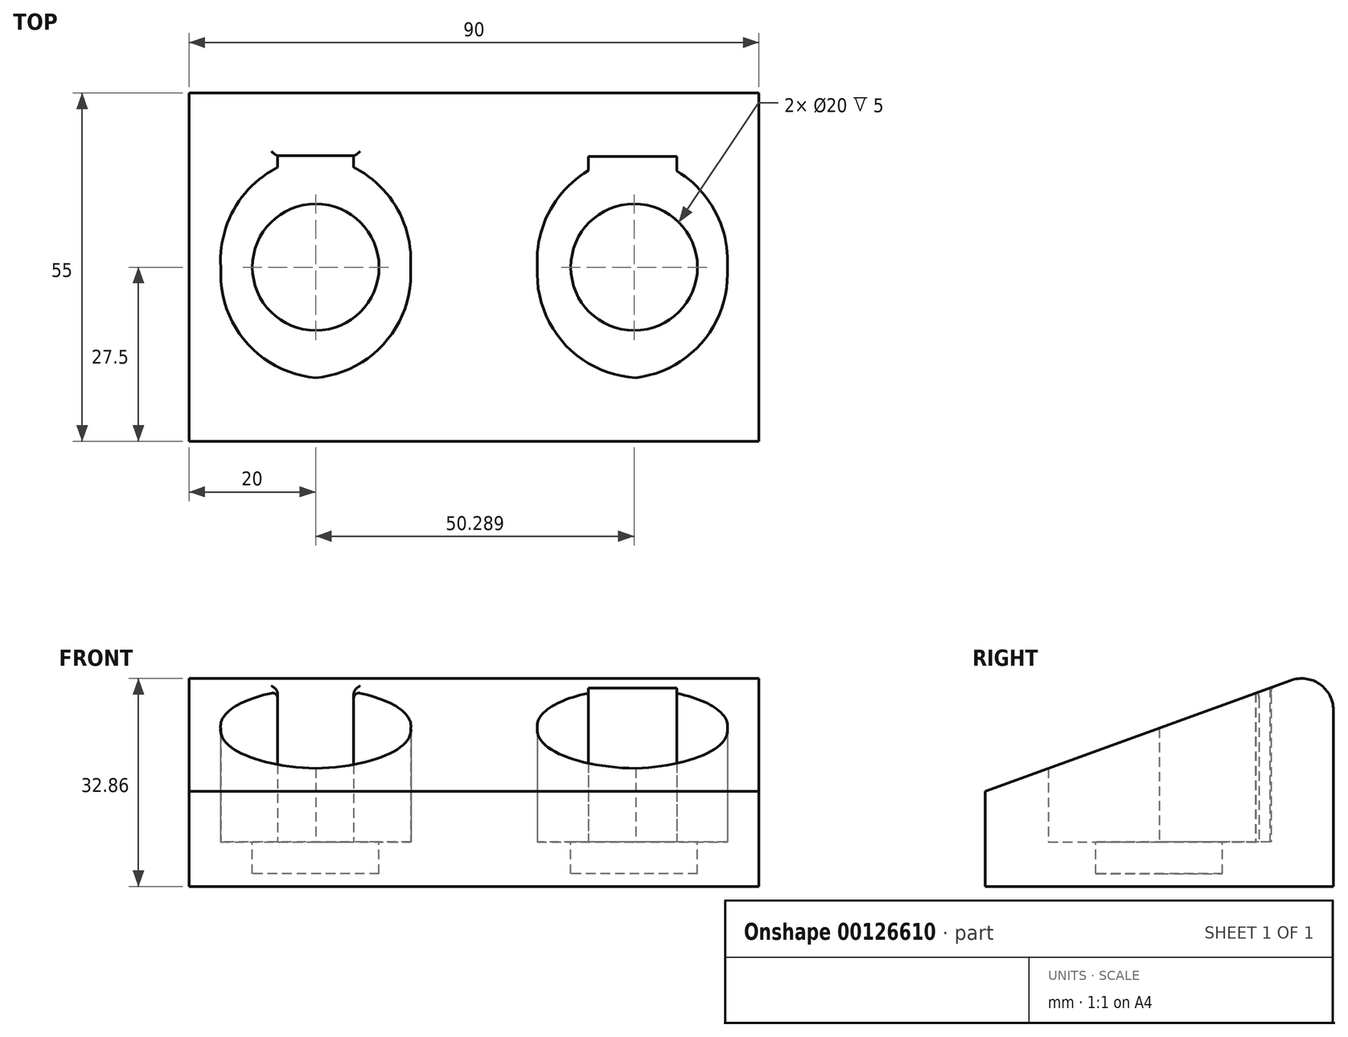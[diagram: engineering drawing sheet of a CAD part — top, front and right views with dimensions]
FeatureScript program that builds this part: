
annotation { "Feature Type Name" : "Feature", "Feature Type Description" : "" }
export const myFeature = defineFeature(function(context is Context, id is Id, definition is map)
    precondition{}
    {
        {
            var Q0;
            Q0=qCreatedBy(makeId("Top.planeOp"),FACE);
            var sketch = newSketch(context, id + "F0", { "sketchPlane" : qUnion([Q0])});
            skLineSegment(sketch, "E0", {"start": v(0, 0) * mm, "end": v(-25, 0) * mm, "construction": true});
            skLineSegment(sketch, "E1", {"start": v(0, 0) * mm, "end": v(25, 0) * mm, "construction": true});
            skLineSegment(sketch, "E2", {"start": v(-25, 0) * mm, "end": v(-10, 0) * mm, "construction": true});
            skLineSegment(sketch, "E3", {"start": v(-25, 0) * mm, "end": v(-25, 24.58) * mm, "construction": true});
            skLineSegment(sketch, "E4", {"start": v(-25, 0) * mm, "end": v(-25, -21.82) * mm, "construction": true});
            skArc(sketch, "E5", {"start": v(-25, 17.5) * mm, "mid": v(-36.06, 11.8) * mm, "end": v(-40, 0) * mm});
            skArc(sketch, "E6", {"start": v(-40, 0) * mm, "mid": v(-36.06, -11.8) * mm, "end": v(-25, -17.5) * mm});
            skArc(sketch, "E7", {"start": v(-10, 0) * mm, "mid": v(-13.94, 11.8) * mm, "end": v(-25, 17.5) * mm});
            skArc(sketch, "E8", {"start": v(-25, -17.5) * mm, "mid": v(-13.94, -11.8) * mm, "end": v(-10, 0) * mm});
            skLineSegment(sketch, "E9", {"start": v(-25, 17.5) * mm, "end": v(32.65, 17.5) * mm, "construction": true});
            skLineSegment(sketch, "E10", {"start": v(-25, -17.5) * mm, "end": v(35.4, -17.5) * mm, "construction": true});
            skLineSegment(sketch, "E11", {"start": v(25, 0) * mm, "end": v(25, 19.84) * mm, "construction": true});
            skLineSegment(sketch, "E12", {"start": v(25, 19.84) * mm, "end": v(25.58, -19.79) * mm, "construction": true});
            skArc(sketch, "E13", {"start": v(25.03, 17.5) * mm, "mid": v(13.95, 11.81) * mm, "end": v(10, 0) * mm});
            skArc(sketch, "E14", {"start": v(10, 0) * mm, "mid": v(14.13, -11.98) * mm, "end": v(25.54, -17.5) * mm});
            skArc(sketch, "E15", {"start": v(40, 0) * mm, "mid": v(36.07, 11.8) * mm, "end": v(25.03, 17.5) * mm});
            skArc(sketch, "E16", {"start": v(25.54, -17.5) * mm, "mid": v(36.26, -11.63) * mm, "end": v(40, 0) * mm});
            skLineSegment(sketch, "E17", {"start": v(0, 0) * mm, "end": v(-45, 0) * mm, "construction": true});
            skLineSegment(sketch, "E18", {"start": v(-45, 0) * mm, "end": v(-45, -27.5) * mm, "construction": true});
            skLineSegment(sketch, "E19", {"start": v(-45, 0) * mm, "end": v(-45, 27.5) * mm, "construction": true});
            skLineSegment(sketch, "E20", {"start": v(0, 0) * mm, "end": v(45, 0) * mm, "construction": true});
            skLineSegment(sketch, "E21", {"start": v(45, 0) * mm, "end": v(45, 27.5) * mm, "construction": true});
            skLineSegment(sketch, "E22.bottom", {"start": v(-45, -27.5) * mm, "end": v(45, -27.5) * mm});
            skLineSegment(sketch, "E22.top", {"start": v(-45, 27.5) * mm, "end": v(45, 27.5) * mm});
            skLineSegment(sketch, "E22.left", {"start": v(-45, -27.5) * mm, "end": v(-45, 27.5) * mm});
            skLineSegment(sketch, "E22.right", {"start": v(45, -27.5) * mm, "end": v(45, 27.5) * mm});
            skSolve(sketch);
        }
        {
            var Q0;
            Q0=makeQuery(id+"F0.imprint","IMPRINT",FACE,{"disambiguationData":[TD([[makeQuery(id+"F0.imprint","IMPRINT",EDGE,{"derivedFrom":sQuery(id+"F0.wireOp",EDGE,"E5")}),-1.0]])]});
            extrude(context, id + "F1", {"entities" : qUnion([Q0]), "depth" : 35 * mm});
        }
        {
            var Q0;
            Q0=makeQuery(id+"F0.imprint","IMPRINT",FACE,{"disambiguationData":[TD([[makeQuery(id+"F0.imprint","IMPRINT",EDGE,{"derivedFrom":sQuery(id+"F0.wireOp",EDGE,"E5")}),1.0]])]});
            var Q1;
            Q1=makeQuery(id+"F0.imprint","IMPRINT",FACE,{"disambiguationData":[TD([[makeQuery(id+"F0.imprint","IMPRINT",EDGE,{"derivedFrom":sQuery(id+"F0.wireOp",EDGE,"E13")}),1.0]])]});
            extrude(context, id + "F2", {"entities" : qUnion([Q0, Q1]), "operationType" : NewBodyOperationType.ADD, "depth" : 7 * mm});
        }
        {
            var Q0;
            Q0=makeQuery(id+"F2.opExtrude","CAP_FACE",FACE,{"disambiguationData":[OSD([sQuery(id+"F0.wireOp",EDGE,"E5"),sQuery(id+"F0.wireOp",EDGE,"E6"),sQuery(id+"F0.wireOp",EDGE,"E7"),sQuery(id+"F0.wireOp",EDGE,"E8")])],"isStart":false});
            var sketch = newSketch(context, id + "F3", { "sketchPlane" : qUnion([Q0])});
            skArc(sketch, "E23.0.0", {"start": v(40, 0) * mm, "mid": v(36.07, 11.8) * mm, "end": v(25.03, 17.5) * mm});
            skArc(sketch, "E23.0.1", {"start": v(25.03, 17.5) * mm, "mid": v(13.95, 11.81) * mm, "end": v(10, 0) * mm});
            skArc(sketch, "E23.0.2", {"start": v(10, 0) * mm, "mid": v(14.13, -11.98) * mm, "end": v(25.54, -17.5) * mm});
            skArc(sketch, "E23.0.3", {"start": v(25.54, -17.5) * mm, "mid": v(36.26, -11.63) * mm, "end": v(40, 0) * mm});
            skLineSegment(sketch, "E24", {"start": v(-25, 17.5) * mm, "end": v(-25, -17.5) * mm, "construction": true});
            skLineSegment(sketch, "E25", {"start": v(-25, -17.5) * mm, "end": v(-40, 0) * mm, "construction": true});
            skLineSegment(sketch, "E26", {"start": v(-40, 0) * mm, "end": v(-10, 0) * mm, "construction": true});
            skLineSegment(sketch, "E27", {"start": v(10, 0) * mm, "end": v(40, 0) * mm, "construction": true});
            skLineSegment(sketch, "E28", {"start": v(25.03, 17.5) * mm, "end": v(25.54, -17.5) * mm, "construction": true});
            skCircle(sketch, "E29", {"center": v(-25, 0) * mm, "radius": 10 * mm, "construction": true});
            skCircle(sketch, "E30", {"center": v(-25, 0) * mm, "radius": 10 * mm});
            skCircle(sketch, "E31", {"center": v(25.29, 0) * mm, "radius": 10 * mm});
            skSolve(sketch);
        }
        {
            var Q0;
            Q0=makeQuery(id+"F3.imprint","IMPRINT",FACE,{"disambiguationData":[TD([[makeQuery(id+"F3.imprint","IMPRINT",EDGE,{"derivedFrom":sQuery(id+"F3.wireOp",EDGE,"E30")}),1.0]])]});
            var Q1;
            Q1=makeQuery(id+"F3.imprint","IMPRINT",FACE,{"disambiguationData":[TD([[makeQuery(id+"F3.imprint","IMPRINT",EDGE,{"derivedFrom":sQuery(id+"F3.wireOp",EDGE,"E31")}),1.0]])]});
            extrude(context, id + "F4", {"entities" : qUnion([Q0, Q1]), "operationType" : NewBodyOperationType.REMOVE, "oppositeDirection" : true, "depth" : 5 * mm});
        }
        {
            var Q0;
            Q0=makeQuery(id+"F1.opExtrude","SWEPT_FACE",FACE,{"disambiguationData":[OSD([sQuery(id+"F0.wireOp",EDGE,"E22.right")])]});
            var sketch = newSketch(context, id + "F5", { "sketchPlane" : qUnion([Q0])});
            skLineSegment(sketch, "E32", {"start": v(-27.5, 0) * mm, "end": v(-27.5, 15) * mm, "construction": true});
            skLineSegment(sketch, "E33", {"start": v(27.5, 35) * mm, "end": v(-27.5, 15) * mm});
            skSolve(sketch);
        }
        {
            var Q0;
            Q0=qSketchRegion(id+"F5",true);
            var Q1;
            {var subQ0=sQuery(id+"F5.wireOp",EDGE,"E33");Q1=makeQuery(id+"F5.imprint","IMPRINT",FACE,{"disambiguationData":[TD([[makeQuery(id+"F5.imprint","IMPRINT",EDGE,{"derivedFrom":subQ0}),-1.0]])]});}
            extrude(context, id + "F6", {"entities" : qUnion([Q0, Q1]), "operationType" : NewBodyOperationType.REMOVE, "oppositeDirection" : true, "depth" : 90 * mm});
        }
        {
            var Q0;
            {var subQ0=sQuery(id+"F0.wireOp",EDGE,"E22.top");Q0=makeQuery(id+"F6.boolean.opBoolean","MERGE",EDGE,{"derivedFrom":[makeQuery(id+"F1.opExtrude","CAP_EDGE",EDGE,{"disambiguationData":[OSD([subQ0])],"isStart":false}),makeQuery(id+"F6.opExtrude","SWEPT_EDGE",EDGE,{"disambiguationData":[OSD([subQ0,sQuery(id+"F0.wireOp",EDGE,"E22.right"),sQuery(id+"F5.wireOp",EDGE,"E33")])]})]});}
            var Q1;
            Q1=makeQuery(id+"F6.boolean.opBoolean","COPY",EDGE,{"derivedFrom":makeQuery(id+"F6.opExtrude","CAP_EDGE",EDGE,{"disambiguationData":[OSD([sQuery(id+"F5.wireOp",EDGE,"E33")])],"isStart":false})});
            var Q2;
            Q2=makeQuery(id+"F6.boolean.opBoolean","COPY",EDGE,{"derivedFrom":makeQuery(id+"F6.opExtrude","SWEPT_EDGE",EDGE,{"disambiguationData":[OSD([sQuery(id+"F0.wireOp",EDGE,"E22.bottom"),sQuery(id+"F0.wireOp",EDGE,"E22.right"),sQuery(id+"F5.wireOp",EDGE,"E33")])]})});
            var Q3;
            Q3=makeQuery(id+"F6.boolean.opBoolean","COPY",EDGE,{"derivedFrom":makeQuery(id+"F6.opExtrude","CAP_EDGE",EDGE,{"disambiguationData":[OSD([sQuery(id+"F5.wireOp",EDGE,"E33")])],"isStart":true})});
            fillet(context, id + "F7", {"entities" : qUnion([Q0, Q1, Q2, Q3]), "radius" : 5 * mm, "tangentPropagation" : true, "allowEdgeOverflow" : false});
        }
        {
            var Q0;
            Q0=makeQuery(id+"F2.opExtrude","CAP_FACE",FACE,{"disambiguationData":[OSD([sQuery(id+"F0.wireOp",EDGE,"E5"),sQuery(id+"F0.wireOp",EDGE,"E6"),sQuery(id+"F0.wireOp",EDGE,"E7"),sQuery(id+"F0.wireOp",EDGE,"E8")])],"isStart":false});
            var sketch = newSketch(context, id + "F8", { "sketchPlane" : qUnion([Q0])});
            skPoint(sketch, "E34.0", {"position": v(25.03, 17.5) * mm});
            skLineSegment(sketch, "E35", {"start": v(-25, 17.5) * mm, "end": v(25.03, 17.5) * mm, "construction": true});
            skLineSegment(sketch, "E36", {"start": v(-16.75, 17.5) * mm, "end": v(-36.03, 17.69) * mm, "construction": true});
            skLineSegment(sketch, "E37", {"start": v(-25, 17.5) * mm, "end": v(-31, 17.64) * mm});
            skLineSegment(sketch, "E38.bottom", {"start": v(-31, 17.64) * mm, "end": v(-19, 17.64) * mm});
            skLineSegment(sketch, "E38.top", {"start": v(-31, 14.64) * mm, "end": v(-19, 14.64) * mm});
            skLineSegment(sketch, "E38.left", {"start": v(-31, 17.64) * mm, "end": v(-31, 14.64) * mm});
            skLineSegment(sketch, "E38.right", {"start": v(-19, 17.64) * mm, "end": v(-19, 14.64) * mm});
            skLineSegment(sketch, "E39", {"start": v(25.03, 17.5) * mm, "end": v(18.03, 17.5) * mm});
            skLineSegment(sketch, "E40.bottom", {"start": v(18.03, 17.5) * mm, "end": v(32.03, 17.5) * mm});
            skLineSegment(sketch, "E40.top", {"start": v(18.03, 14.5) * mm, "end": v(32.03, 14.5) * mm});
            skLineSegment(sketch, "E40.left", {"start": v(18.03, 17.5) * mm, "end": v(18.03, 14.5) * mm});
            skLineSegment(sketch, "E40.right", {"start": v(32.03, 17.5) * mm, "end": v(32.03, 14.5) * mm});
            skSolve(sketch);
        }
        {
            var Q0;
            Q0 = qSketchRegion(id + "F8", true);
            extrude(context, id + "F9", {"entities" : qUnion([Q0]), "operationType" : NewBodyOperationType.REMOVE, "depth" : 30.7 * mm, "offsetDistance" : 25 * mm});
        }
        {
            var Q0;
            Q0=makeQuery(id+"F9.boolean.opBoolean","INTERSECT",EDGE,{"derivedFrom":[makeQuery(id+"F6.boolean.opBoolean","COPY",FACE,{"derivedFrom":makeQuery(id+"F6.opExtrude","SWEPT_FACE",FACE,{"disambiguationData":[OSD([sQuery(id+"F5.wireOp",EDGE,"E33")])]})}),makeQuery(id+"F9.opExtrude","SWEPT_FACE",FACE,{"disambiguationData":[OSD([sQuery(id+"F8.wireOp",EDGE,"E38.bottom")])]})]});
            var Q1;
            Q1=makeQuery(id+"F9.boolean.opBoolean","INTERSECT",EDGE,{"derivedFrom":[makeQuery(id+"F6.boolean.opBoolean","COPY",FACE,{"derivedFrom":makeQuery(id+"F6.opExtrude","SWEPT_FACE",FACE,{"disambiguationData":[OSD([sQuery(id+"F5.wireOp",EDGE,"E33")])]})}),makeQuery(id+"F9.opExtrude","SWEPT_FACE",FACE,{"disambiguationData":[OSD([sQuery(id+"F8.wireOp",EDGE,"xXgQVaRy-Ccnl-1kDg-ZfZx-vEKaDnwB0KKw.bottom")])]})]});
            var Q2;
            Q2=makeQuery(id+"F9.boolean.opBoolean","INTERSECT",EDGE,{"derivedFrom":[makeQuery(id+"F6.boolean.opBoolean","COPY",FACE,{"derivedFrom":makeQuery(id+"F6.opExtrude","SWEPT_FACE",FACE,{"disambiguationData":[OSD([sQuery(id+"F5.wireOp",EDGE,"E33")])]})}),makeQuery(id+"F9.opExtrude","SWEPT_FACE",FACE,{"disambiguationData":[OSD([sQuery(id+"F8.wireOp",EDGE,"xXgQVaRy-Ccnl-1kDg-ZfZx-vEKaDnwB0KKw.right")])]})]});
            var Q3;
            Q3=makeQuery(id+"F9.boolean.opBoolean","INTERSECT",EDGE,{"derivedFrom":[makeQuery(id+"F6.boolean.opBoolean","COPY",FACE,{"derivedFrom":makeQuery(id+"F6.opExtrude","SWEPT_FACE",FACE,{"disambiguationData":[OSD([sQuery(id+"F5.wireOp",EDGE,"E33")])]})}),makeQuery(id+"F9.opExtrude","SWEPT_FACE",FACE,{"disambiguationData":[OSD([sQuery(id+"F8.wireOp",EDGE,"xXgQVaRy-Ccnl-1kDg-ZfZx-vEKaDnwB0KKw.left")])]})]});
            var Q4;
            Q4=makeQuery(id+"F9.boolean.opBoolean","INTERSECT",EDGE,{"derivedFrom":[makeQuery(id+"F6.boolean.opBoolean","COPY",FACE,{"derivedFrom":makeQuery(id+"F6.opExtrude","SWEPT_FACE",FACE,{"disambiguationData":[OSD([sQuery(id+"F5.wireOp",EDGE,"E33")])]})}),makeQuery(id+"F9.opExtrude","SWEPT_FACE",FACE,{"disambiguationData":[OSD([sQuery(id+"F8.wireOp",EDGE,"E38.left")])]})]});
            var Q5;
            Q5=makeQuery(id+"F9.boolean.opBoolean","INTERSECT",EDGE,{"derivedFrom":[makeQuery(id+"F6.boolean.opBoolean","COPY",FACE,{"derivedFrom":makeQuery(id+"F6.opExtrude","SWEPT_FACE",FACE,{"disambiguationData":[OSD([sQuery(id+"F5.wireOp",EDGE,"E33")])]})}),makeQuery(id+"F9.opExtrude","SWEPT_FACE",FACE,{"disambiguationData":[OSD([sQuery(id+"F8.wireOp",EDGE,"E38.right")])]})]});
            fillet(context, id + "F10", {"entities" : qUnion([Q0, Q1, Q2, Q3, Q4, Q5]), "radius" : 1 * mm, "tangentPropagation" : true, "allowEdgeOverflow" : false});
        }
    });
